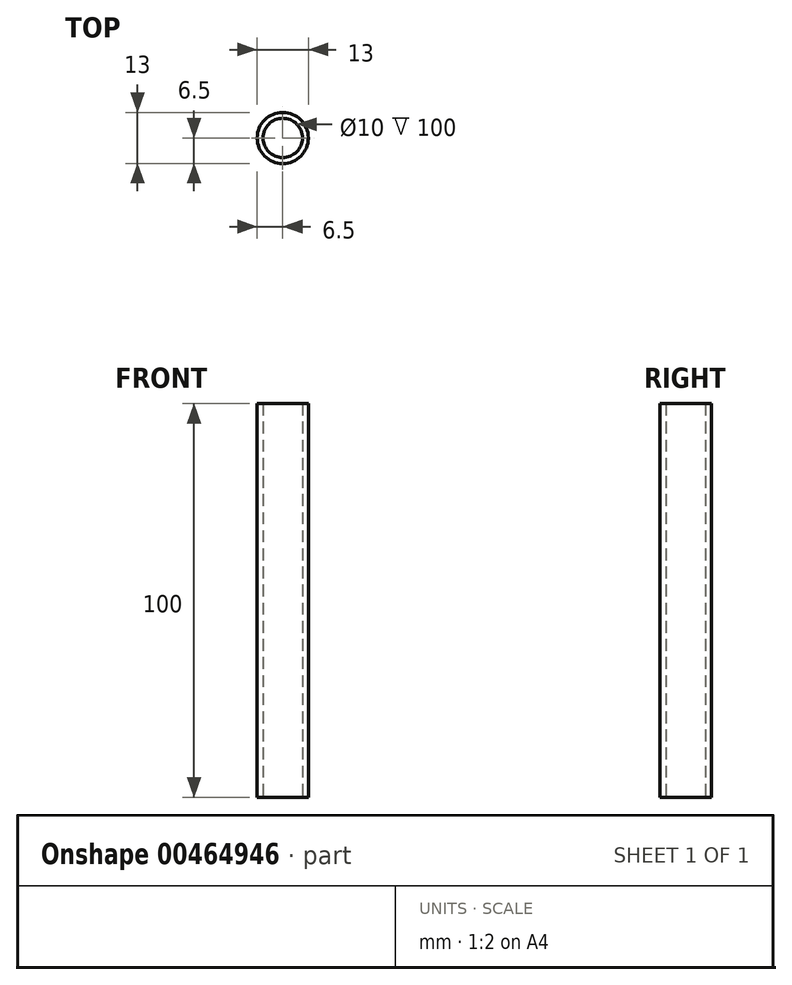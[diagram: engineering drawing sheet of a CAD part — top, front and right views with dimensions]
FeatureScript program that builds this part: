
annotation { "Feature Type Name" : "Feature", "Feature Type Description" : "" }
export const myFeature = defineFeature(function(context is Context, id is Id, definition is map)
    precondition{}
    {
        {
            var Q0;
            Q0=qCreatedBy(makeId("Top.planeOp"),FACE);
            var sketch = newSketch(context, id + "F0", { "sketchPlane" : qUnion([Q0])});
            skCircle(sketch, "E0", {"center": v(0, 0) * mm, "radius": 6.5 * mm});
            skCircle(sketch, "E1", {"center": v(0, 0) * mm, "radius": 5 * mm});
            skSolve(sketch);
        }
        {
            var Q0;
            Q0=qSketchRegion(id+"F0",true);
            extrude(context, id + "F1", {"entities" : qUnion([Q0]), "depth" : 100 * mm});
        }
    });
